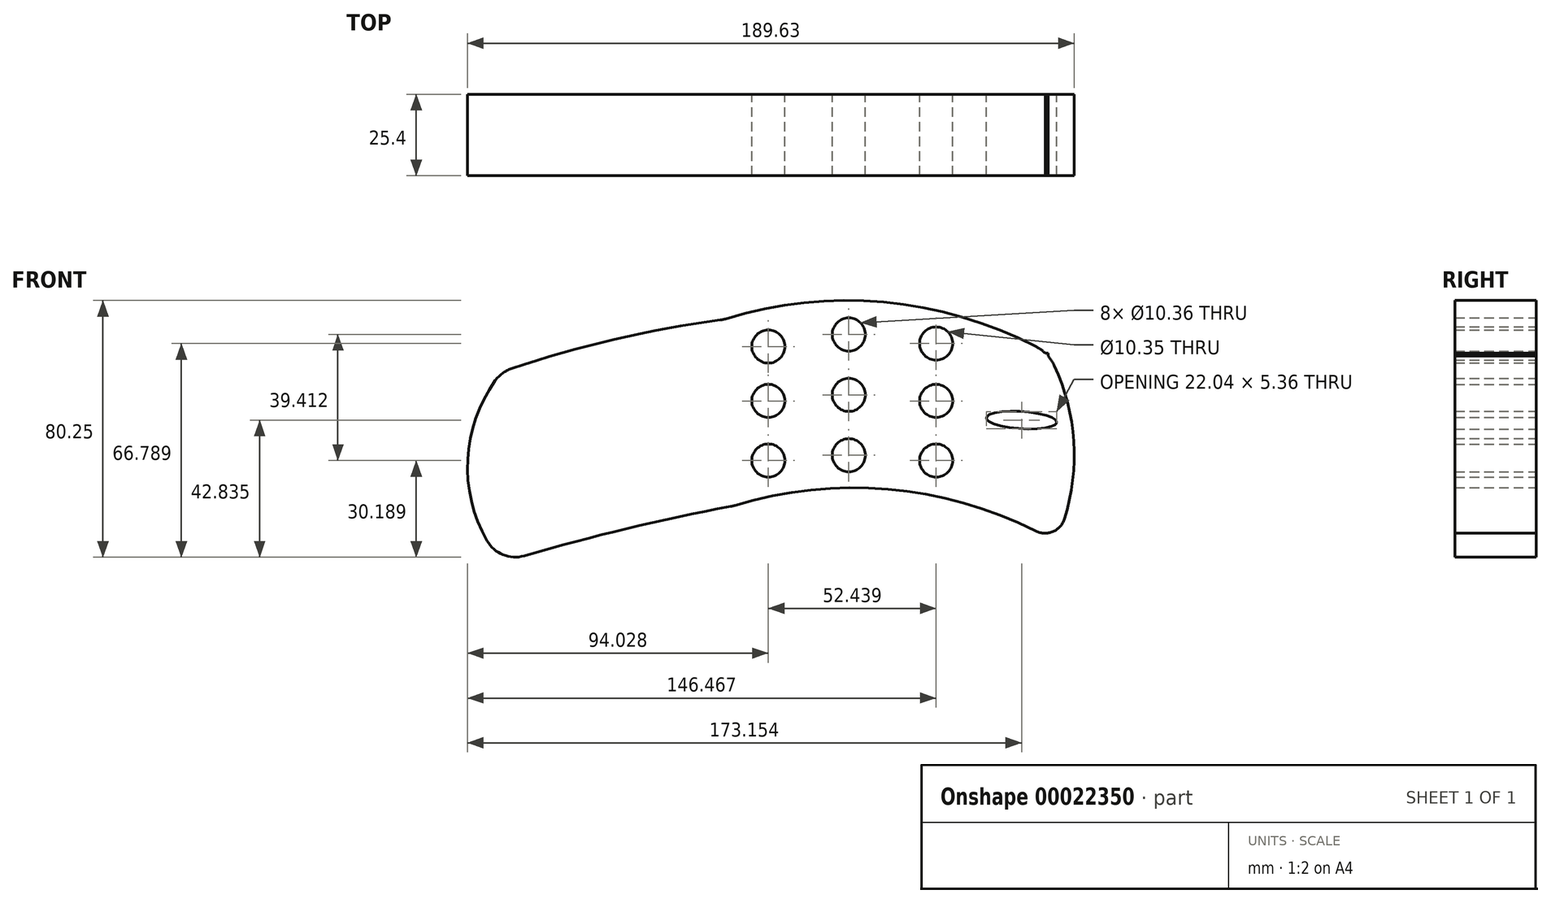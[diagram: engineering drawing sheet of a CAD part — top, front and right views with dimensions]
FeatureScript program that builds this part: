
annotation { "Feature Type Name" : "Feature", "Feature Type Description" : "" }
export const myFeature = defineFeature(function(context is Context, id is Id, definition is map)
    precondition{}
    {
        {
            var Q0;
            Q0=qCreatedBy(makeId("Front.planeOp"),FACE);
            var sketch = newSketch(context, id + "F0", { "sketchPlane" : qUnion([Q0])});
            skArc(sketch, "E0", {"start": v(66.07, 3.47) * mm, "mid": v(19.82, 16.55) * mm, "end": v(-27.98, 11.5) * mm});
            skPoint(sketch, "E1.visualSharp", {"position": v(-54.5, 0) * mm});
            skLineSegment(sketch, "E2", {"start": v(69, 59.1) * mm, "end": v(69.86, 59.1) * mm});
            skArc(sketch, "E3", {"start": v(66.21, 61.08) * mm, "mid": v(18.5, 75.06) * mm, "end": v(-30.95, 69.82) * mm});
            skPoint(sketch, "E4.visualSharp", {"position": v(-55.8, 59.1) * mm});
            skArc(sketch, "E5", {"start": v(74.98, 7.23) * mm, "mid": v(77.93, 31.5) * mm, "end": v(71.84, 55.2) * mm});
            skPoint(sketch, "E6.visualSharp", {"position": v(72.27, 0.14) * mm});
            skArc(sketch, "E6.filletArc", {"start": v(66.07, 3.47) * mm, "mid": v(71.4, 3.3) * mm, "end": v(74.98, 7.23) * mm});
            skPoint(sketch, "E7.visualSharp", {"position": v(69.86, 59.1) * mm});
            skArc(sketch, "E7.filletArc", {"start": v(71.84, 55.2) * mm, "mid": v(69.51, 58.6) * mm, "end": v(66.21, 61.08) * mm});
            skArc(sketch, "E8", {"start": v(42.7, 12.46) * mm, "mid": v(46.08, 41.44) * mm, "end": v(42.92, 70.44) * mm});
            skArc(sketch, "E9", {"start": v(-28.63, 11.3) * mm, "mid": v(-26.34, 40.64) * mm, "end": v(-31.75, 69.56) * mm});
            skCircle(sketch, "E10", {"center": v(34.9, 62.12) * mm, "radius": 5.18 * mm});
            skCircle(sketch, "E11", {"center": v(34.9, 44.17) * mm, "radius": 5.18 * mm});
            skCircle(sketch, "E12", {"center": v(34.9, 25.52) * mm, "radius": 5.18 * mm});
            skCircle(sketch, "E13", {"center": v(7.61, 64.93) * mm, "radius": 5.18 * mm});
            skCircle(sketch, "E14", {"center": v(7.61, 46.06) * mm, "radius": 5.18 * mm});
            skCircle(sketch, "E15", {"center": v(7.61, 27.2) * mm, "radius": 5.18 * mm});
            skCircle(sketch, "E16", {"center": v(-17.53, 61.17) * mm, "radius": 5.18 * mm});
            skPoint(sketch, "E17.center.orphan", {"position": v(-17.53, 63.5) * mm});
            skCircle(sketch, "E18", {"center": v(-17.53, 44.17) * mm, "radius": 5.18 * mm});
            skCircle(sketch, "E19", {"center": v(-17.53, 25.52) * mm, "radius": 5.18 * mm});
            skArc(sketch, "E20", {"start": v(-32.6, 69.45) * mm, "mid": v(-65.6, 63.4) * mm, "end": v(-97.85, 54.24) * mm});
            skPoint(sketch, "E21.visualSharp", {"position": v(-31.75, 69.56) * mm});
            skArc(sketch, "E21.filletArc", {"start": v(-32.6, 69.45) * mm, "mid": v(-31.77, 69.6) * mm, "end": v(-30.95, 69.82) * mm});
            skArc(sketch, "E22", {"start": v(-29.33, 11.18) * mm, "mid": v(-61.76, 4.25) * mm, "end": v(-93.8, -4.26) * mm});
            skPoint(sketch, "E23.visualSharp", {"position": v(-28.63, 11.3) * mm});
            skArc(sketch, "E23.filletArc", {"start": v(-29.33, 11.18) * mm, "mid": v(-28.65, 11.32) * mm, "end": v(-27.98, 11.5) * mm});
            skArc(sketch, "E24", {"start": v(-102.87, 50.52) * mm, "mid": v(-111.5, 25.88) * mm, "end": v(-105.49, 0.47) * mm});
            skPoint(sketch, "E25.visualSharp", {"position": v(-100.77, 53.25) * mm});
            skArc(sketch, "E25.filletArc", {"start": v(-97.85, 54.24) * mm, "mid": v(-100.66, 52.78) * mm, "end": v(-102.87, 50.52) * mm});
            skPoint(sketch, "E26.visualSharp", {"position": v(-100.77, -6.33) * mm});
            skArc(sketch, "E26.filletArc", {"start": v(-105.49, 0.47) * mm, "mid": v(-100.47, -3.92) * mm, "end": v(-93.8, -4.26) * mm});
            skLineSegment(sketch, "E27", {"start": v(69.86, 59.1) * mm, "end": v(69.88, 58.2) * mm});
            skPoint(sketch, "E28.orphan", {"position": v(71.4, 3.3) * mm});
            skLineSegment(sketch, "E29", {"start": v(69.86, 59.1) * mm, "end": v(69.86, 58.22) * mm});
            skPoint(sketch, "E30.orphan", {"position": v(69.88, 31.4) * mm});
            skPoint(sketch, "E31.start.orphan", {"position": v(77.93, 31.4) * mm});
            skEllipse(sketch, "E32", {"center": v(61.6, 38.16) * mm, "majorRadius": 11.04 * mm, "minorRadius": 2.68 * mm, "majorAxis": v(1, -0.06)});
            skPoint(sketch, "E33.start.orphan", {"position": v(50.57, 38.85) * mm});
            skPoint(sketch, "E34.end.orphan", {"position": v(72.62, 37.48) * mm});
            skLineSegment(sketch, "E35", {"start": v(72.62, 37.48) * mm, "end": v(77.26, 37.48) * mm});
            skPoint(sketch, "E36.visualSharp", {"position": v(-90.58, -17.7) * mm});
            skSolve(sketch);
        }
        {
            var Q0;
            Q0 = qSketchRegion(id + "F0", true);
            extrude(context, id + "F1", {"entities" : qUnion([Q0]), "depth" : 25.4 * mm});
        }
    });
